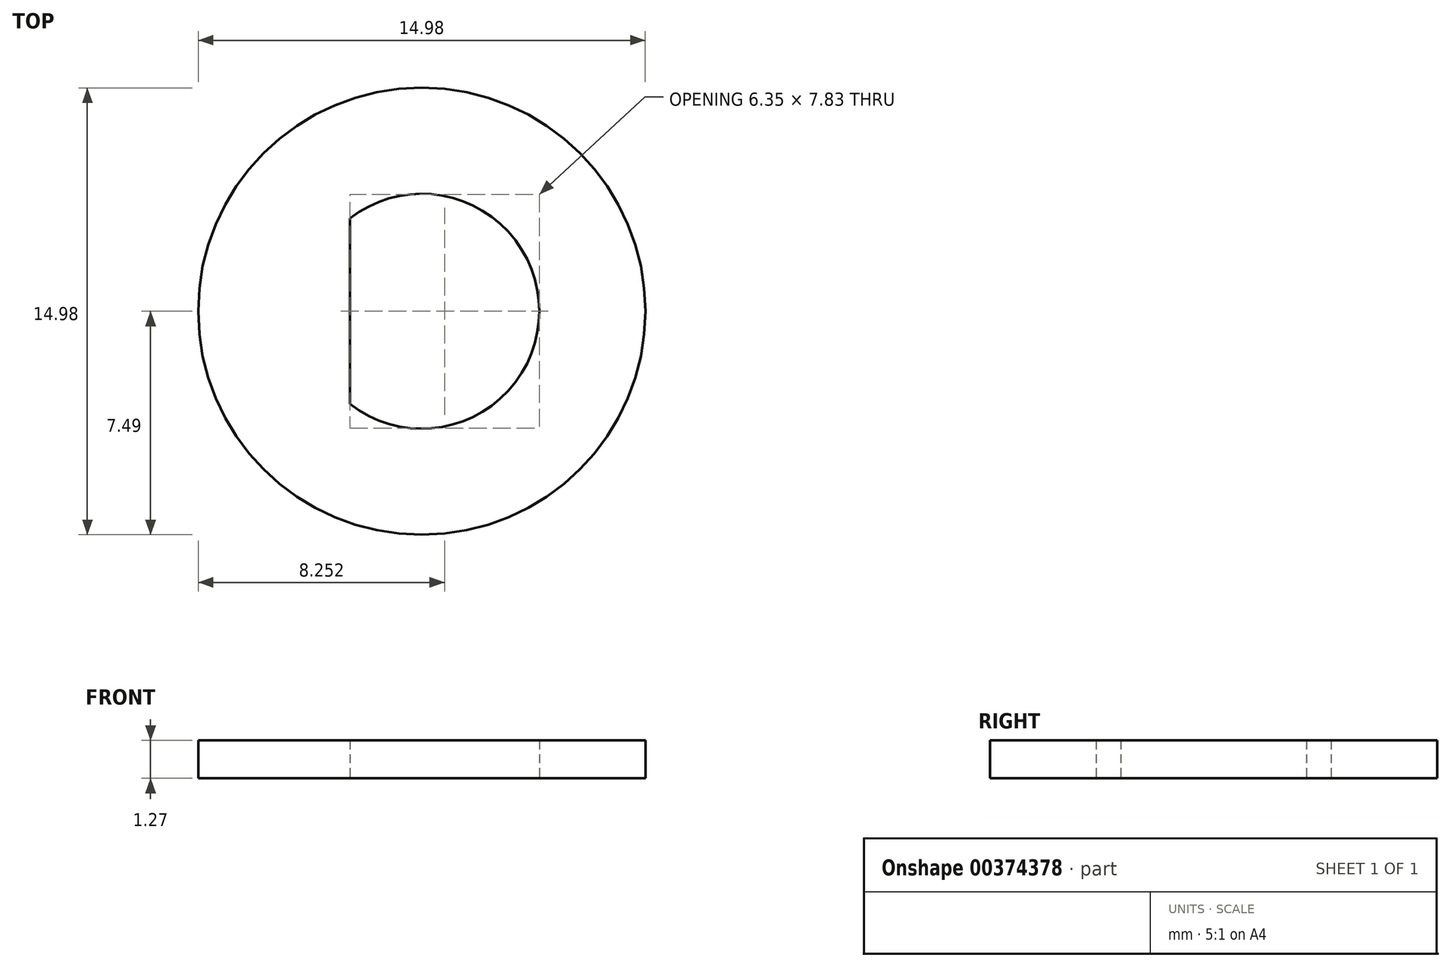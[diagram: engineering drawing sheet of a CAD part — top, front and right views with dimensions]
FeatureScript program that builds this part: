
annotation { "Feature Type Name" : "Feature", "Feature Type Description" : "" }
export const myFeature = defineFeature(function(context is Context, id is Id, definition is map)
    precondition{}
    {
        {
            var Q0;
            Q0=qCreatedBy(makeId("Top.planeOp"),FACE);
            var sketch = newSketch(context, id + "F0", { "sketchPlane" : qUnion([Q0])});
            skArc(sketch, "E0", {"start": v(-2.41, -3.11) * mm, "mid": v(3.94, 0) * mm, "end": v(-2.41, 3.11) * mm});
            skCircle(sketch, "E1", {"center": v(0, 0) * mm, "radius": 7.5 * mm});
            skLineSegment(sketch, "E2", {"start": v(-2.41, 3.11) * mm, "end": v(-2.41, -3.11) * mm});
            skSolve(sketch);
        }
        {
            var Q0;
            Q0=makeQuery(id+"F0.imprint","IMPRINT",FACE,{"disambiguationData":[TD([[makeQuery(id+"F0.imprint","IMPRINT",EDGE,{"derivedFrom":sQuery(id+"F0.wireOp",EDGE,"E0")}),-1.0]])]});
            extrude(context, id + "F1", {"entities" : qUnion([Q0]), "depth" : 1.27 * mm});
        }
    });
